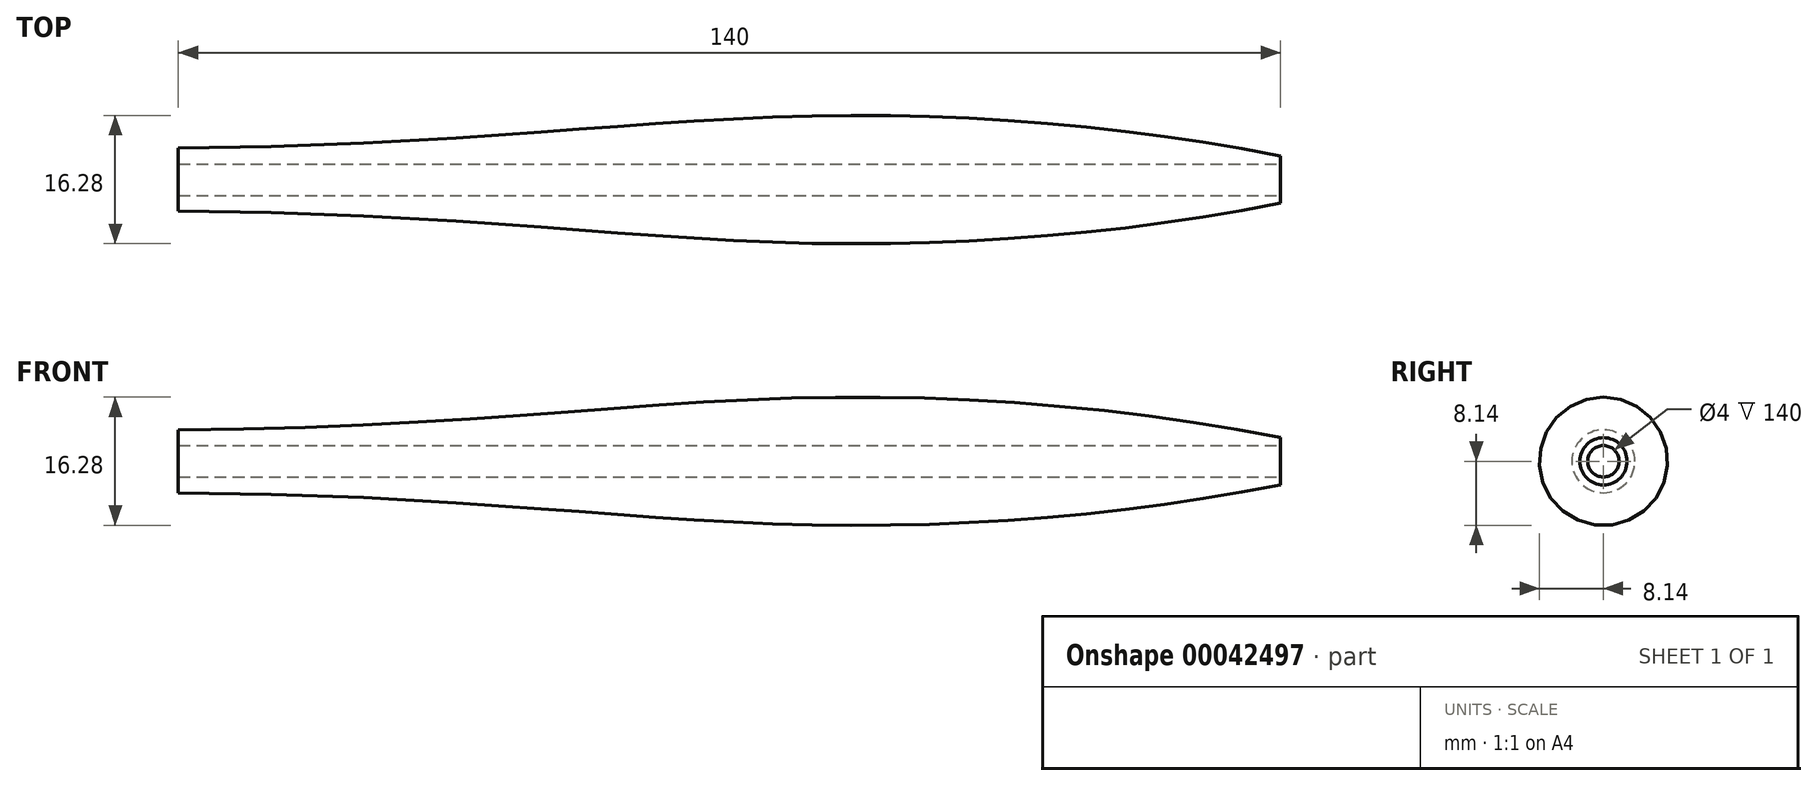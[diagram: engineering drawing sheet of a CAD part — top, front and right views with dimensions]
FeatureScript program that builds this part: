
annotation { "Feature Type Name" : "Feature", "Feature Type Description" : "" }
export const myFeature = defineFeature(function(context is Context, id is Id, definition is map)
    precondition{}
    {
        {
            var Q0;
            Q0=qCreatedBy(makeId("Front.planeOp"),FACE);
            var sketch = newSketch(context, id + "F0", { "sketchPlane" : qUnion([Q0])});
            skLineSegment(sketch, "E0", {"start": v(0, 0) * mm, "end": v(140, 0) * mm});
            skLineSegment(sketch, "E1", {"start": v(140, 0) * mm, "end": v(140, 3) * mm});
            skLineSegment(sketch, "E2", {"start": v(0, 0) * mm, "end": v(0, 4) * mm});
            skFitSpline(sketch, "E3", {"points": [v(140, 3) * mm, v(79.33, 8.06) * mm, v(0, 4) * mm], "startDerivative": vector(-125.98, 25.09) * mm, "endDerivative": vector(-196.83, -1.1) * mm});
            skSolve(sketch);
        }
        {
            var Q0;
            Q0=makeQuery(id+"F0.imprint","IMPRINT",FACE,{"disambiguationData":[TD([[makeQuery(id+"F0.imprint","IMPRINT",EDGE,{"derivedFrom":sQuery(id+"F0.wireOp",EDGE,"E0")}),1.0]])]});
            var Q1;
            Q1=sQuery(id+"F0.wireOp",EDGE,"E0");
            revolve(context, id + "F1", {"entities" : qUnion([Q0]), "axis" : qUnion([Q1]), "revolveType" : RevolveType.FULL});
        }
        {
            var Q0;
            Q0=makeQuery(id+"F1.opRevolve","SWEPT_FACE",FACE,{"disambiguationData":[OSD([sQuery(id+"F0.wireOp",EDGE,"E1")])]});
            var sketch = newSketch(context, id + "F2", { "sketchPlane" : qUnion([Q0])});
            skCircle(sketch, "E4", {"center": v(0, 0) * mm, "radius": 2 * mm});
            skSolve(sketch);
        }
        {
            var Q0;
            Q0 = qSketchRegion(id + "F2", true);
            extrude(context, id + "F3", {"entities" : qUnion([Q0]), "operationType" : NewBodyOperationType.REMOVE, "endBound" : BoundingType.THROUGH_ALL, "oppositeDirection" : true, "depth" : 25 * mm});
        }
    });
